# Revit family: SANINDUSA_140113004LM_Urb.y_sidewatersupplyconnectioncisternwithdualflushmechanismforclosecoupledtoilet365x170x435_V0
name_source: partatom
category: Plumbing Fixtures
revit_build: Autodesk Revit 2018 (Build: 20170223_1515(x64)
units: mm (PartAtom-declared; Revit-internal decimal feet)

## family parameters
Cut with Voids When Loaded = No
Host = Face
Part Type = Normal
Room Calculation Point = No
Round Connector Dimension = Use Diameter
Shared = No

## types (1)
- SANINDUSA_140113004LM_Urb.y_sidewatersupplyconnectioncisternwithdualflushmechanismforclosecoupledtoilet365x170x435_V0
    AssetType = Fixed
    CisternCapacity = 6 Lts
    CisternHeight = LowLevel
    CisternMaterial = Vitreous China
    Color = white
    Constituents = Ceramic cistern with side inlet connection and dual flush mechanism included.
    Default Elevation = 1219 mm
    Description = A water storage unit attached to a sanitary terminal that is fitted with a device, operated automatically or by the user, that discharges water to cleanse a water closet (toilet) pan, urinal or slop hopper. (BS6100 330 5008)
    Features = Cistern with flushing mechanism for close-coupled toilet.Flushing cistern volume: 6 liters. Mounting for dual flush. Large flush: 6 L. Small flush: 3 L. Connection to the water supply: on the side.
    Finish = gloss
    FlushRate = "Lowerbound:3 Lts
Upperbound:6 Lts"
    FlushType = push
    Installation Instructions = https://www.tec.sanindusa.pt
    InstallationDate = 1900-12-31T23:59:59
    IsAutomaticFlush = FALSE
    IsSingleFlush = FALSE
    Manufacturer = Sanindusa
    ManufacturerName = Sanindusa
    ManufacturerURL = www.tec.sanindusa.pt
    Material = cistern-vitreous china
    Model = 140113004LM
    ModelNumber = 140113004LM
    ModelReference = Urb.y
    Name = 65 Urb.y cistern with dual flush mechanism
    NominalHeight = 435 mm  [stored 1.42717 ft]
    NominalLength = 380 mm
    NominalWidth = 170 mm  [stored 0.557743 ft]
    ProductInformation = https://www.tec.sanindusa.pt
    ProductionYear = 2015
    Size = 365x170x435
    Type (IFC) = IfcSanitaryTerminalType
    URL = www.tec.sanindusa.pt
    WarrantyDescription = https://www.tec.sanindusa.pt
    WarrantyDurationParts = 5
    WarrantyDurationUnit = year
    WarrantyStartDate = 1900-12-31T23:59:59
    Waste Connection = Yes
    Water Supply = 10 mm  [stored 0.0328084 ft]
    Weight = 16.85 kg

note: [stored X ft] marks values corroborated as IEEE doubles in the binary element streams (Revit-internal decimal feet)

## geometry (parser evidence)
native form markers: Sweep x5
no freeform markers — native parametric forms only
